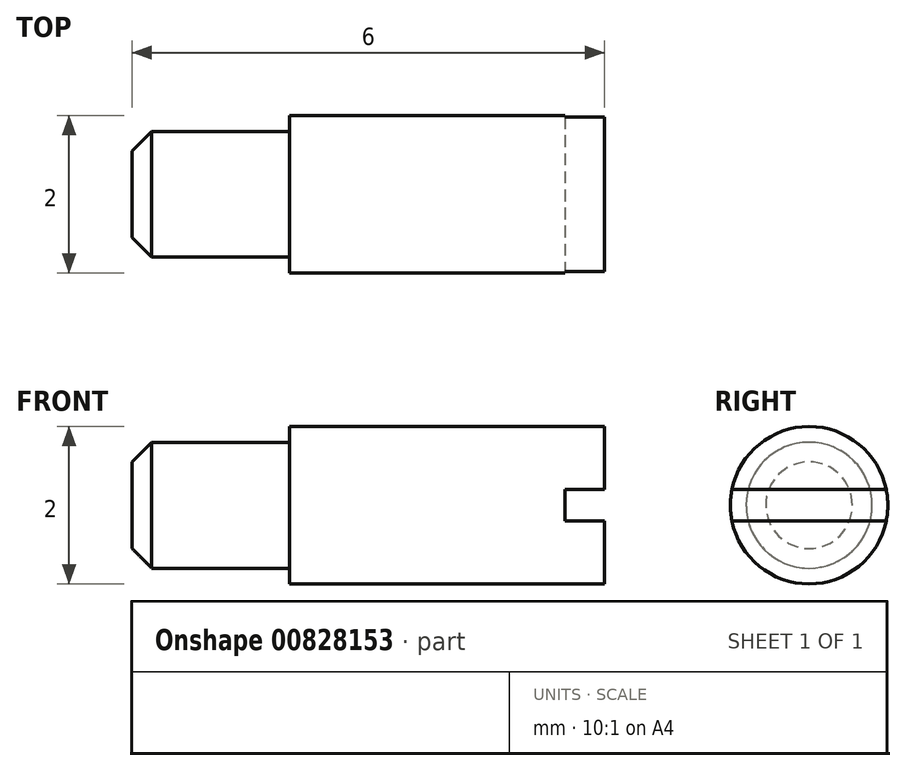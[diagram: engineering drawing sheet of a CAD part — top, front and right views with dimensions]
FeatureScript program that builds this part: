
annotation { "Feature Type Name" : "Feature", "Feature Type Description" : "" }
export const myFeature = defineFeature(function(context is Context, id is Id, definition is map)
    precondition{}
    {
        {
            var Q0;
            Q0=qCreatedBy(makeId("Front.planeOp"),FACE);
            var sketch = newSketch(context, id + "F0", { "sketchPlane" : qUnion([Q0])});
            skLineSegment(sketch, "E0", {"start": v(0, 0) * mm, "end": v(6, 0) * mm});
            skLineSegment(sketch, "E1", {"start": v(6, 0) * mm, "end": v(6, 1) * mm});
            skLineSegment(sketch, "E2", {"start": v(6, 1) * mm, "end": v(2, 1) * mm});
            skLineSegment(sketch, "E3", {"start": v(2, 1) * mm, "end": v(2, 0.8) * mm});
            skLineSegment(sketch, "E4", {"start": v(2, 0.8) * mm, "end": v(0, 0.8) * mm});
            skLineSegment(sketch, "E5", {"start": v(0, 0.8) * mm, "end": v(0, 0) * mm});
            skSolve(sketch);
        }
        {
            var Q0;
            Q0 = qSketchRegion(id + "F0", true);
            var Q1;
            Q1=sQuery(id+"F0.wireOp",EDGE,"E0");
            revolve(context, id + "F1", {"surfaceOperationType" : NewSurfaceOperationType.NEW, "entities" : qUnion([Q0]), "axis" : qUnion([Q1]), "revolveType" : RevolveType.FULL});
        }
        {
            var Q0;
            Q0=makeQuery(id+"F1.opRevolve","SWEPT_EDGE",EDGE,{"disambiguationData":[OSD([sQuery(id+"F0.wireOp",EDGE,"E4"),sQuery(id+"F0.wireOp",EDGE,"E5")])]});
            chamfer(context, id + "F2", {"entities" : qUnion([Q0]), "width" : 0.25 * mm, "tangentPropagation" : true});
        }
        {
            var Q0;
            Q0=qCreatedBy(makeId("Front.planeOp"),FACE);
            var sketch = newSketch(context, id + "F3", { "sketchPlane" : qUnion([Q0])});
            skLineSegment(sketch, "E6.bottom", {"start": v(5.5, 0.2) * mm, "end": v(7, 0.2) * mm});
            skLineSegment(sketch, "E6.top", {"start": v(5.5, -0.2) * mm, "end": v(7, -0.2) * mm});
            skLineSegment(sketch, "E6.left", {"start": v(5.5, 0.2) * mm, "end": v(5.5, -0.2) * mm});
            skLineSegment(sketch, "E6.right", {"start": v(7, 0.2) * mm, "end": v(7, -0.2) * mm});
            skPoint(sketch, "E6.middle", {"position": v(6.25, 0) * mm});
            skSolve(sketch);
        }
        {
            var Q0;
            Q0 = qSketchRegion(id + "F3", true);
            extrude(context, id + "F4", {"entities" : qUnion([Q0]), "operationType" : NewBodyOperationType.REMOVE, "endBound" : BoundingType.SYMMETRIC, "oppositeDirection" : true, "depth" : 25 * mm, "offsetDistance" : 25 * mm});
        }
    });
